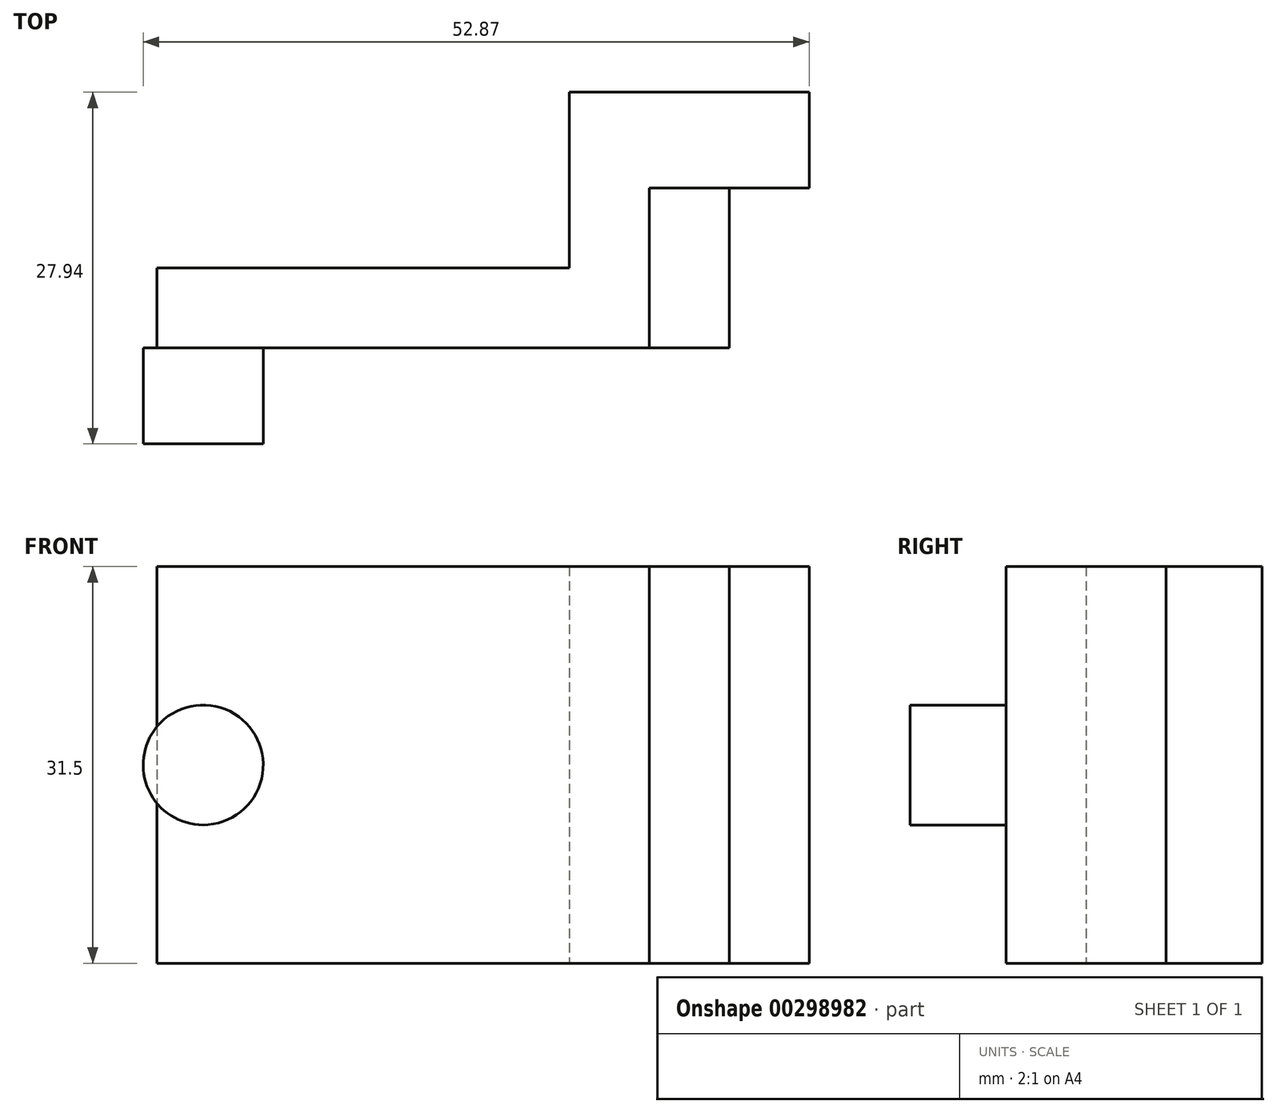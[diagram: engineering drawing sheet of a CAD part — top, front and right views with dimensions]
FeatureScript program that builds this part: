
annotation { "Feature Type Name" : "Feature", "Feature Type Description" : "" }
export const myFeature = defineFeature(function(context is Context, id is Id, definition is map)
    precondition{}
    {
        {
            var Q0;
            Q0=qCreatedBy(makeId("Front.planeOp"),FACE);
            var sketch = newSketch(context, id + "F0", { "sketchPlane" : qUnion([Q0])});
            skCircle(sketch, "E0", {"center": v(0, 0) * mm, "radius": 4.76 * mm});
            skLineSegment(sketch, "E1.bottom", {"start": v(3.66, 3.05) * mm, "end": v(-3.66, 3.05) * mm});
            skLineSegment(sketch, "E1.top", {"start": v(3.66, -3.05) * mm, "end": v(-3.66, -3.05) * mm});
            skLineSegment(sketch, "E1.left", {"start": v(3.66, 3.05) * mm, "end": v(3.66, -3.05) * mm});
            skLineSegment(sketch, "E1.right", {"start": v(-3.66, 3.05) * mm, "end": v(-3.66, -3.05) * mm});
            skSolve(sketch);
        }
        {
            var Q0;
            Q0 = qSketchRegion(id + "F0", true);
            extrude(context, id + "F1", {"entities" : qUnion([Q0]), "depth" : 7.62 * mm});
        }
        {
            var Q0;
            Q0=makeQuery(id+"F0.imprint","IMPRINT",FACE,{"disambiguationData":[TD([[makeQuery(id+"F0.imprint","IMPRINT",EDGE,{"derivedFrom":sQuery(id+"F0.wireOp",EDGE,"E1.bottom")}),1.0]])]});
            extrude(context, id + "F2", {"entities" : qUnion([Q0]), "operationType" : NewBodyOperationType.ADD, "oppositeDirection" : true, "depth" : 6.35 * mm});
        }
        {
            var Q0;
            Q0=makeQuery(id+"F2.opExtrude","SWEPT_FACE",FACE,{"disambiguationData":[OSD([sQuery(id+"F0.wireOp",EDGE,"E1.left")])]});
            extrude(context, id + "F3", {"entities" : qUnion([Q0]), "operationType" : NewBodyOperationType.ADD, "depth" : 25.4 * mm});
        }
        {
            var Q0;
            Q0=makeQuery(id+"F3.opExtrude","CAP_FACE",FACE,{"disambiguationData":[OSD([sQuery(id+"F0.wireOp",EDGE,"E1.left")])],"isStart":false});
            extrude(context, id + "F4", {"entities" : qUnion([Q0]), "depth" : 6.35 * mm});
        }
        {
            var Q0;
            {var subQ0=sQuery(id+"F0.wireOp",EDGE,"E1.left");Q0=makeQuery(id+"F4.opExtrude","SWEPT_FACE",FACE,{"disambiguationData":[OSD([subQ0]),TDD([makeQuery(id+"F3.opExtrude","CAP_EDGE",EDGE,{"disambiguationData":[OSD([subQ0]),TDD([makeQuery(id+"F2.opExtrude","CAP_EDGE",EDGE,{"disambiguationData":[OSD([subQ0])],"isStart":true})])],"isStart":false})])]});}
            extrude(context, id + "F5", {"entities" : qUnion([Q0]), "operationType" : NewBodyOperationType.ADD, "depth" : 6.35 * mm});
        }
        {
            var Q0;
            Q0=makeQuery(id+"F5.opExtrude","CAP_FACE",FACE,{"disambiguationData":[OSD([sQuery(id+"F0.wireOp",EDGE,"E1.left")])],"isStart":false});
            extrude(context, id + "F6", {"entities" : qUnion([Q0]), "depth" : 7.62 * mm});
        }
        {
            var Q0;
            {var subQ0=sQuery(id+"F0.wireOp",EDGE,"E1.left");Q0=makeQuery(id+"F6.opExtrude","SWEPT_FACE",FACE,{"disambiguationData":[OSD([subQ0]),TDD([makeQuery(id+"F5.opExtrude","CAP_EDGE",EDGE,{"disambiguationData":[OSD([subQ0]),TDD([makeQuery(id+"F4.opExtrude","CAP_EDGE",EDGE,{"disambiguationData":[OSD([subQ0]),TDD([makeQuery(id+"F3.opExtrude","CAP_EDGE",EDGE,{"disambiguationData":[OSD([subQ0]),TDD([makeQuery(id+"F2.opExtrude","CAP_EDGE",EDGE,{"disambiguationData":[OSD([subQ0])],"isStart":true})])],"isStart":false})])],"isStart":false})])],"isStart":false})])]});}
            extrude(context, id + "F7", {"entities" : qUnion([Q0]), "operationType" : NewBodyOperationType.ADD, "depth" : 12.7 * mm});
        }
        {
            var Q0;
            {var subQ0=sQuery(id+"F0.wireOp",EDGE,"E1.left");var subQ1=sQuery(id+"F0.wireOp",EDGE,"E1.top");var subQ2=sQuery(id+"F0.wireOp",EDGE,"E0");Q0=makeQuery(id+"F7.boolean.opBoolean","MERGE",FACE,{"derivedFrom":[makeQuery(id+"F6.opExtrude","SWEPT_FACE",FACE,{"disambiguationData":[OSD([subQ2,subQ1,subQ0])]}),makeQuery(id+"F7.opExtrude","SWEPT_FACE",FACE,{"disambiguationData":[OSD([subQ2,subQ1,subQ0])]})]});}
            extrude(context, id + "F8", {"entities" : qUnion([Q0]), "operationType" : NewBodyOperationType.ADD, "depth" : 12.7 * mm});
        }
        {
            var Q0;
            {var subQ0=sQuery(id+"F0.wireOp",EDGE,"E1.left");var subQ1=sQuery(id+"F0.wireOp",EDGE,"E1.bottom");var subQ2=sQuery(id+"F0.wireOp",EDGE,"E0");Q0=makeQuery(id+"F7.boolean.opBoolean","MERGE",FACE,{"derivedFrom":[makeQuery(id+"F6.opExtrude","SWEPT_FACE",FACE,{"disambiguationData":[OSD([subQ2,subQ1,subQ0])]}),makeQuery(id+"F7.opExtrude","SWEPT_FACE",FACE,{"disambiguationData":[OSD([subQ2,subQ1,subQ0])]})]});}
            extrude(context, id + "F9", {"entities" : qUnion([Q0]), "operationType" : NewBodyOperationType.ADD, "depth" : 12.7 * mm});
        }
        {
            var Q0;
            {var subQ0=sQuery(id+"F0.wireOp",EDGE,"E1.left");Q0=makeQuery(id+"F5.boolean.opBoolean","MERGE",FACE,{"derivedFrom":[makeQuery(id+"F4.opExtrude","CAP_FACE",FACE,{"disambiguationData":[OSD([subQ0])],"isStart":false}),makeQuery(id+"F5.opExtrude","SWEPT_FACE",FACE,{"disambiguationData":[OSD([subQ0]),TDD([makeQuery(id+"F4.opExtrude","CAP_EDGE",EDGE,{"disambiguationData":[OSD([subQ0]),TDD([makeQuery(id+"F3.opExtrude","CAP_EDGE",EDGE,{"disambiguationData":[OSD([subQ0]),TDD([makeQuery(id+"F2.opExtrude","CAP_EDGE",EDGE,{"disambiguationData":[OSD([subQ0])],"isStart":true})])],"isStart":false})])],"isStart":false})])]})]});}
            extrude(context, id + "F10", {"entities" : qUnion([Q0]), "depth" : 6.35 * mm});
        }
        {
            var Q0;
            {var subQ0=sQuery(id+"F0.wireOp",EDGE,"E1.left");var subQ1=sQuery(id+"F0.wireOp",EDGE,"E1.bottom");var subQ2=sQuery(id+"F0.wireOp",EDGE,"E0");var subQ3=sQuery(id+"F0.wireOp",EDGE,"E1.top");Q0=makeQuery(id+"F9.boolean.opBoolean","MERGE",FACE,{"derivedFrom":[makeQuery(id+"F8.boolean.opBoolean","MERGE",FACE,{"derivedFrom":[makeQuery(id+"F7.boolean.opBoolean","MERGE",FACE,{"derivedFrom":[makeQuery(id+"F6.opExtrude","CAP_FACE",FACE,{"disambiguationData":[OSD([subQ0])],"isStart":true}),makeQuery(id+"F7.opExtrude","SWEPT_FACE",FACE,{"disambiguationData":[OSD([subQ0]),TDD([makeQuery(id+"F6.opExtrude","CAP_EDGE",EDGE,{"disambiguationData":[OSD([subQ0]),TDD([makeQuery(id+"F5.opExtrude","CAP_EDGE",EDGE,{"disambiguationData":[OSD([subQ0]),TDD([makeQuery(id+"F4.opExtrude","CAP_EDGE",EDGE,{"disambiguationData":[OSD([subQ0]),TDD([makeQuery(id+"F3.opExtrude","CAP_EDGE",EDGE,{"disambiguationData":[OSD([subQ0]),TDD([makeQuery(id+"F2.opExtrude","CAP_EDGE",EDGE,{"disambiguationData":[OSD([subQ0])],"isStart":true})])],"isStart":false})])],"isStart":false})])],"isStart":false})])],"isStart":true})])]})]}),makeQuery(id+"F8.opExtrude","SWEPT_FACE",FACE,{"disambiguationData":[OSD([subQ2,subQ3,subQ0]),TDD([makeQuery(id+"F7.boolean.opBoolean","MERGE",EDGE,{"derivedFrom":[makeQuery(id+"F6.opExtrude","CAP_EDGE",EDGE,{"disambiguationData":[OSD([subQ2,subQ3,subQ0])],"isStart":true}),makeQuery(id+"F7.opExtrude","SWEPT_EDGE",EDGE,{"disambiguationData":[OSD([subQ2,subQ3,subQ0]),TDD([makeQuery(id+"F6.opExtrude","CAP_VERTEX",VERTEX,{"disambiguationData":[OSD([subQ2,subQ3,subQ0]),TDD([makeQuery(id+"F5.opExtrude","CAP_VERTEX",VERTEX,{"disambiguationData":[OSD([subQ2,subQ3,subQ0]),TDD([makeQuery(id+"F4.opExtrude","CAP_VERTEX",VERTEX,{"disambiguationData":[OSD([subQ2,subQ3,subQ0]),TDD([makeQuery(id+"F3.opExtrude","CAP_VERTEX",VERTEX,{"disambiguationData":[OSD([subQ2,subQ3,subQ0]),TDD([makeQuery(id+"F2.opExtrude","CAP_VERTEX",VERTEX,{"disambiguationData":[OSD([subQ2,subQ3,subQ0])],"isStart":true})])],"isStart":false})])],"isStart":false})])],"isStart":false})])],"isStart":true})])]})]})])]})]}),makeQuery(id+"F9.opExtrude","SWEPT_FACE",FACE,{"disambiguationData":[OSD([subQ2,subQ1,subQ0]),TDD([makeQuery(id+"F7.boolean.opBoolean","MERGE",EDGE,{"derivedFrom":[makeQuery(id+"F6.opExtrude","CAP_EDGE",EDGE,{"disambiguationData":[OSD([subQ2,subQ1,subQ0])],"isStart":true}),makeQuery(id+"F7.opExtrude","SWEPT_EDGE",EDGE,{"disambiguationData":[OSD([subQ2,subQ1,subQ0]),TDD([makeQuery(id+"F6.opExtrude","CAP_VERTEX",VERTEX,{"disambiguationData":[OSD([subQ2,subQ1,subQ0]),TDD([makeQuery(id+"F5.opExtrude","CAP_VERTEX",VERTEX,{"disambiguationData":[OSD([subQ2,subQ1,subQ0]),TDD([makeQuery(id+"F4.opExtrude","CAP_VERTEX",VERTEX,{"disambiguationData":[OSD([subQ2,subQ1,subQ0]),TDD([makeQuery(id+"F3.opExtrude","CAP_VERTEX",VERTEX,{"disambiguationData":[OSD([subQ2,subQ1,subQ0]),TDD([makeQuery(id+"F2.opExtrude","CAP_VERTEX",VERTEX,{"disambiguationData":[OSD([subQ2,subQ1,subQ0])],"isStart":true})])],"isStart":false})])],"isStart":false})])],"isStart":false})])],"isStart":true})])]})]})])]})]});}
            var sketch = newSketch(context, id + "F11", { "sketchPlane" : qUnion([Q0])});
            skCircle(sketch, "E2", {"center": v(-36.77, 8.82) * mm, "radius": 3.18 * mm});
            skCircle(sketch, "E3.MirrorC", {"center": v(-36.77, -8.82) * mm, "radius": 3.18 * mm});
            skSolve(sketch);
        }
        {
            var Q0;
            Q0=makeQuery(id+"F11.imprint","IMPRINT",FACE,{"disambiguationData":[TD([[makeQuery(id+"F11.imprint","IMPRINT",EDGE,{"derivedFrom":sQuery(id+"F11.wireOp",EDGE,"E2")}),1.0]])]});
            var Q1;
            Q1=makeQuery(id+"F11.imprint","IMPRINT",FACE,{"disambiguationData":[TD([[makeQuery(id+"F11.imprint","IMPRINT",EDGE,{"derivedFrom":sQuery(id+"F11.wireOp",EDGE,"E3.MirrorC")}),-1.0]])]});
            extrude(context, id + "F12", {"entities" : qUnion([Q0, Q1]), "operationType" : NewBodyOperationType.REMOVE, "oppositeDirection" : true, "depth" : 25.4 * mm});
        }
    });
